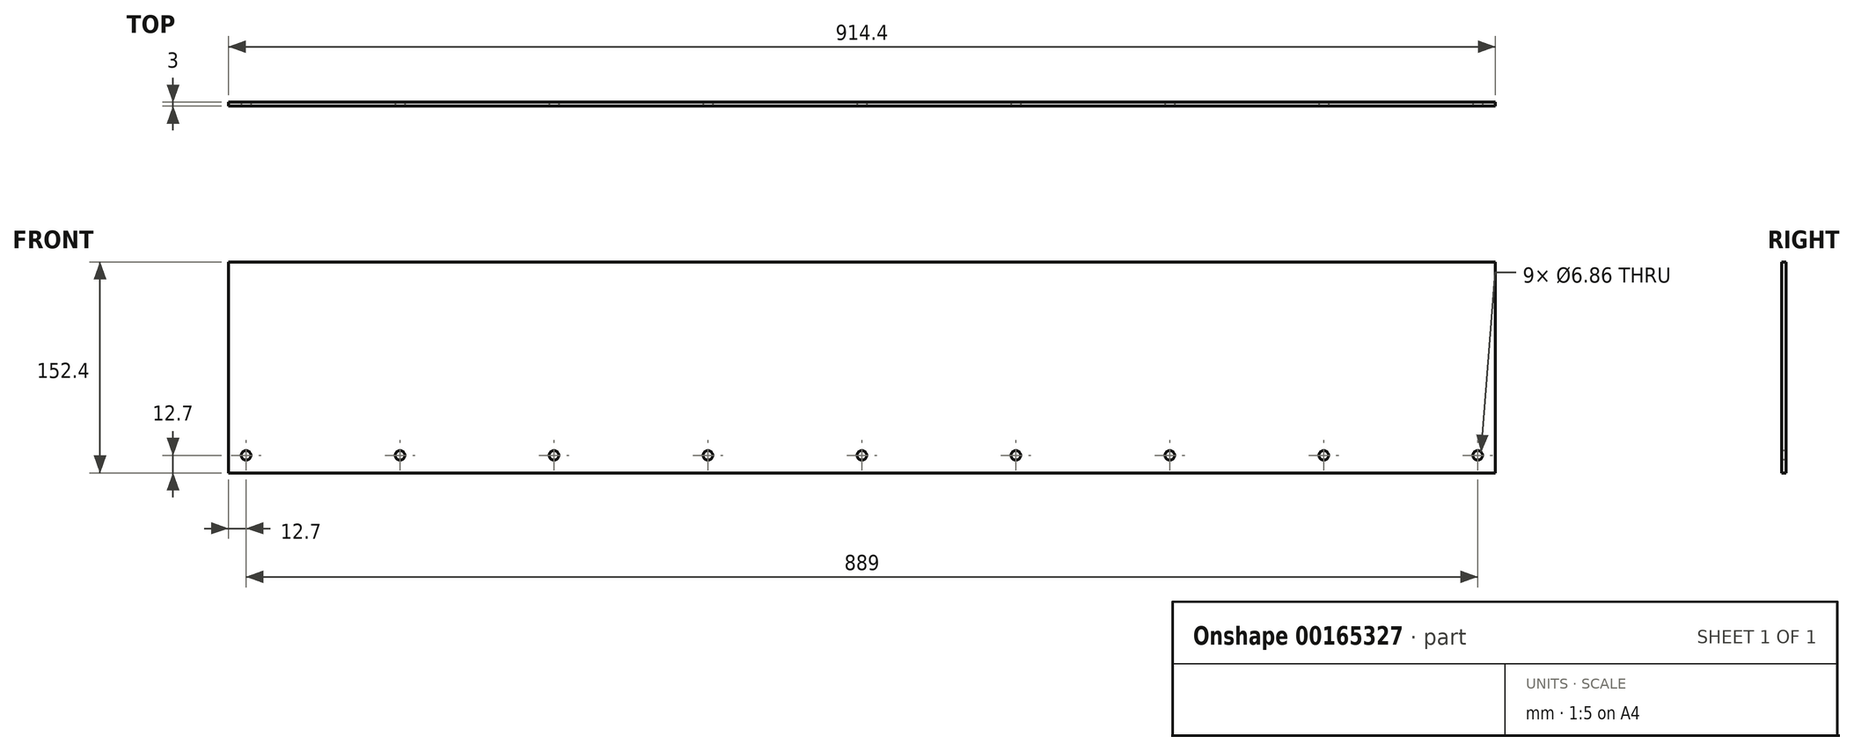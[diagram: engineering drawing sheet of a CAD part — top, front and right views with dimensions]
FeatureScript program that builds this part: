
annotation { "Feature Type Name" : "Feature", "Feature Type Description" : "" }
export const myFeature = defineFeature(function(context is Context, id is Id, definition is map)
    precondition{}
    {
        {
            var Q0;
            Q0=qCreatedBy(makeId("Front.planeOp"),FACE);
            var sketch = newSketch(context, id + "F0", { "sketchPlane" : qUnion([Q0])});
            skLineSegment(sketch, "E0.bottom", {"start": v(457.2, -76.2) * mm, "end": v(-457.2, -76.2) * mm});
            skLineSegment(sketch, "E0.top", {"start": v(457.2, 76.2) * mm, "end": v(-457.2, 76.2) * mm});
            skLineSegment(sketch, "E0.left", {"start": v(457.2, -76.2) * mm, "end": v(457.2, 76.2) * mm});
            skLineSegment(sketch, "E0.right", {"start": v(-457.2, -76.2) * mm, "end": v(-457.2, 76.2) * mm});
            skPoint(sketch, "E0.middle", {"position": v(0, 0) * mm});
            skSolve(sketch);
        }
        {
            var Q0;
            Q0 = qSketchRegion(id + "F0", true);
            extrude(context, id + "F1", {"entities" : qUnion([Q0]), "depth" : 3 * mm});
        }
        {
            var Q0;
            Q0=makeQuery(id+"F1.opExtrude","CAP_FACE",FACE,{"disambiguationData":[OSD([sQuery(id+"F0.wireOp",EDGE,"E0.bottom"),sQuery(id+"F0.wireOp",EDGE,"E0.top"),sQuery(id+"F0.wireOp",EDGE,"E0.left"),sQuery(id+"F0.wireOp",EDGE,"E0.right")])],"isStart":false});
            var sketch = newSketch(context, id + "F2", { "sketchPlane" : qUnion([Q0])});
            skLineSegment(sketch, "E1", {"start": v(-457.2, -63.5) * mm, "end": v(457.2, -63.5) * mm, "construction": true});
            skLineSegment(sketch, "E2", {"start": v(-444.5, 76.2) * mm, "end": v(-444.5, -76.2) * mm, "construction": true});
            skLineSegment(sketch, "E3", {"start": v(444.5, 76.2) * mm, "end": v(444.5, -76.2) * mm, "construction": true});
            skLineSegment(sketch, "E4", {"start": v(0, -76.2) * mm, "end": v(0, 76.2) * mm, "construction": true});
            skLineSegment(sketch, "E5", {"start": v(-222.25, 76.2) * mm, "end": v(-222.25, -76.2) * mm, "construction": true});
            skLineSegment(sketch, "E6", {"start": v(-111.13, 76.2) * mm, "end": v(-111.13, -76.2) * mm, "construction": true});
            skLineSegment(sketch, "E7", {"start": v(-333.38, 76.2) * mm, "end": v(-333.38, -76.2) * mm, "construction": true});
            skLineSegment(sketch, "E8", {"start": v(111.12, 76.2) * mm, "end": v(111.13, -76.2) * mm, "construction": true});
            skLineSegment(sketch, "E9", {"start": v(222.25, 76.2) * mm, "end": v(222.25, -76.2) * mm, "construction": true});
            skLineSegment(sketch, "E10", {"start": v(333.38, 76.2) * mm, "end": v(333.38, -76.2) * mm, "construction": true});
            skCircle(sketch, "E11", {"center": v(-444.5, -63.5) * mm, "radius": 3.43 * mm});
            skCircle(sketch, "E12", {"center": v(-333.38, -63.5) * mm, "radius": 3.43 * mm});
            skCircle(sketch, "E13", {"center": v(-222.25, -63.5) * mm, "radius": 3.43 * mm});
            skCircle(sketch, "E14", {"center": v(-111.13, -63.5) * mm, "radius": 3.43 * mm});
            skCircle(sketch, "E15", {"center": v(0, -63.5) * mm, "radius": 3.43 * mm});
            skCircle(sketch, "E16", {"center": v(111.13, -63.5) * mm, "radius": 3.43 * mm});
            skCircle(sketch, "E17", {"center": v(222.25, -63.5) * mm, "radius": 3.43 * mm});
            skCircle(sketch, "E18", {"center": v(333.38, -63.5) * mm, "radius": 3.43 * mm});
            skCircle(sketch, "E19", {"center": v(444.5, -63.5) * mm, "radius": 3.43 * mm});
            skSolve(sketch);
        }
        {
            var Q0;
            Q0 = qSketchRegion(id + "F2", true);
            extrude(context, id + "F3", {"entities" : qUnion([Q0]), "operationType" : NewBodyOperationType.REMOVE, "endBound" : BoundingType.THROUGH_ALL, "oppositeDirection" : true, "depth" : 25.4 * mm});
        }
    });
